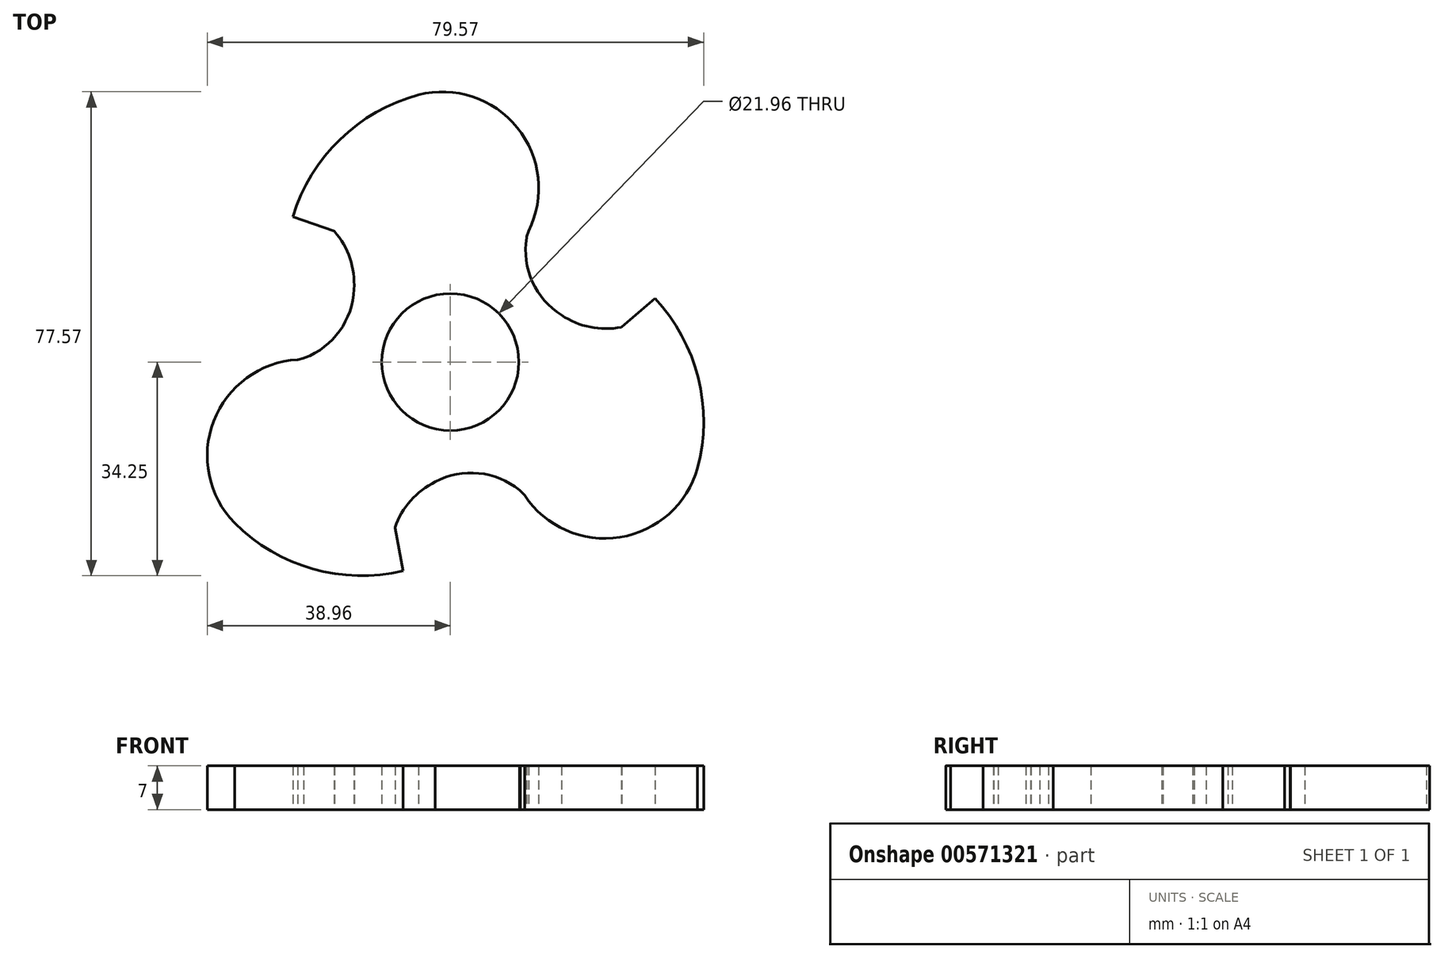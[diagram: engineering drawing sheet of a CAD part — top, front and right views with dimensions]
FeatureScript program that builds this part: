
annotation { "Feature Type Name" : "Feature", "Feature Type Description" : "" }
export const myFeature = defineFeature(function(context is Context, id is Id, definition is map)
    precondition{}
    {
        {
            var Q0;
            Q0=qCreatedBy(makeId("Top.planeOp"),FACE);
            var sketch = newSketch(context, id + "F0", { "sketchPlane" : qUnion([Q0])});
            skCircle(sketch, "E0", {"center": v(0, 0) * mm, "radius": 10.98 * mm});
            skPoint(sketch, "E1.start.orphan", {"position": v(0, 43.22) * mm});
            skPoint(sketch, "E2.2.0.end.orphan", {"position": v(32.77, 10.17) * mm});
            skPoint(sketch, "E3.orphan", {"position": v(11.11, -20.52) * mm});
            skPoint(sketch, "E4.trimOffspring.end.orphan", {"position": v(27.48, 5.59) * mm});
            skPoint(sketch, "E5.orphan", {"position": v(-8.9, -26.47) * mm});
            skPoint(sketch, "E6.orphan", {"position": v(-18.61, 21.02) * mm});
            skPoint(sketch, "E7.2.0", {"position": v(-23.33, 0.64) * mm});
            skArc(sketch, "E7.2.2", {"start": v(-23.36, 0.67) * mm, "mid": v(-17.74, 4.99) * mm, "end": v(-15.44, 11.7) * mm});
            skArc(sketch, "E7.2.3", {"start": v(-15.44, 11.7) * mm, "mid": v(-16.08, 16.63) * mm, "end": v(-18.56, 20.95) * mm});
            skLineSegment(sketch, "E7.2.4", {"start": v(-18.64, 21) * mm, "end": v(-25.23, 23.3) * mm});
            skLineSegment(sketch, "E7.2.5", {"start": v(-18.56, 20.95) * mm, "end": v(-18.64, 21) * mm});
            skArc(sketch, "E7.2.6", {"start": v(-5.1, 42.84) * mm, "mid": v(-17.7, 35.68) * mm, "end": v(-25.23, 23.3) * mm});
            skArc(sketch, "E7.2.7", {"start": v(12.54, 21) * mm, "mid": v(10.72, 37.58) * mm, "end": v(-5.1, 42.84) * mm});
            skPoint(sketch, "E8.orphan", {"position": v(12.77, 20.88) * mm});
            skPoint(sketch, "E9.1.3.end.orphan", {"position": v(-7.57, -33.47) * mm});
            skPoint(sketch, "E10.center", {"position": v(-0.02, -0.02) * mm});
            skPoint(sketch, "E11.orphan", {"position": v(12.23, 19.85) * mm});
            skPoint(sketch, "E12.orphan", {"position": v(32.77, 10.14) * mm});
            skLineSegment(sketch, "E13", {"start": v(-23.36, 0.67) * mm, "end": v(-23.52, 0.6) * mm});
            skPoint(sketch, "E14.orphan", {"position": v(-23.37, 0.63) * mm});
            skArc(sketch, "E15.1.2", {"start": v(11.1, -20.55) * mm, "mid": v(4.55, -17.84) * mm, "end": v(-2.4, -19.2) * mm});
            skArc(sketch, "E15.1.3", {"start": v(-2.4, -19.2) * mm, "mid": v(-6.36, -22.22) * mm, "end": v(-8.86, -26.52) * mm});
            skLineSegment(sketch, "E15.1.4", {"start": v(-8.87, -26.62) * mm, "end": v(-7.57, -33.48) * mm});
            skArc(sketch, "E15.1.5", {"start": v(-34.57, -25.8) * mm, "mid": v(-22.07, -33.15) * mm, "end": v(-7.57, -33.48) * mm});
            skArc(sketch, "E15.1.6", {"start": v(-24.49, 0.39) * mm, "mid": v(-37.93, -9.48) * mm, "end": v(-34.57, -25.8) * mm});
            skLineSegment(sketch, "E15.1.7", {"start": v(-24.49, 0.39) * mm, "end": v(-23.52, 0.6) * mm});
            skLineSegment(sketch, "E15.2.0", {"start": v(12.53, 20.98) * mm, "end": v(12.25, 20.09) * mm});
            skLineSegment(sketch, "E15.2.1", {"start": v(12.22, 19.9) * mm, "end": v(12.25, 20.09) * mm});
            skArc(sketch, "E15.2.2", {"start": v(12.22, 19.9) * mm, "mid": v(13.15, 12.87) * mm, "end": v(17.81, 7.52) * mm});
            skArc(sketch, "E15.2.3", {"start": v(17.81, 7.52) * mm, "mid": v(22.41, 5.6) * mm, "end": v(27.4, 5.59) * mm});
            skLineSegment(sketch, "E15.2.4", {"start": v(27.5, 5.63) * mm, "end": v(32.78, 10.18) * mm});
            skArc(sketch, "E15.2.5", {"start": v(39.63, -17.01) * mm, "mid": v(39.73, -2.53) * mm, "end": v(32.78, 10.18) * mm});
            skArc(sketch, "E15.2.6", {"start": v(11.9, -21.38) * mm, "mid": v(27.17, -28.09) * mm, "end": v(39.63, -17.01) * mm});
            skLineSegment(sketch, "E15.2.7", {"start": v(11.9, -21.38) * mm, "end": v(11.22, -20.63) * mm});
            skPoint(sketch, "E16.orphan", {"position": v(12.22, 19.89) * mm});
            skLineSegment(sketch, "E17", {"start": v(12.54, 21) * mm, "end": v(12.53, 20.98) * mm});
            skPoint(sketch, "E18.orphan", {"position": v(12.55, 21.05) * mm});
            skLineSegment(sketch, "E19", {"start": v(11.1, -20.55) * mm, "end": v(11.22, -20.63) * mm});
            skPoint(sketch, "E20.orphan", {"position": v(10.91, -20.39) * mm});
            skPoint(sketch, "E21.orphan", {"position": v(-23.11, 0.75) * mm});
            skPoint(sketch, "E22.orphan", {"position": v(-23.54, 0.6) * mm});
            skLineSegment(sketch, "E23", {"start": v(-8.86, -26.52) * mm, "end": v(-8.87, -26.62) * mm});
            skLineSegment(sketch, "E24", {"start": v(27.4, 5.59) * mm, "end": v(27.5, 5.63) * mm});
            skArc(sketch, "E25", {"start": v(8.57, 22.3) * mm, "mid": v(9.96, 9.86) * mm, "end": v(20.9, 3.8) * mm});
            skSolve(sketch);
        }
        {
            var Q0;
            Q0=qSketchRegion(id+"F0",true);
            extrude(context, id + "F1", {"entities" : qUnion([Q0]), "depth" : 7 * mm, "offsetDistance" : 25 * mm});
        }
    });
